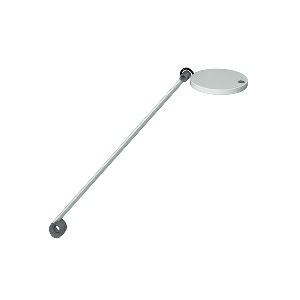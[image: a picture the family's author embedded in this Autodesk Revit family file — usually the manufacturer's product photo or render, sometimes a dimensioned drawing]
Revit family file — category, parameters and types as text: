
# Revit family: para_mi_-_mftl_102_r__940_00643982_8d90
name_source: partatom
category: Lighting Fixtures
units: mm (PartAtom-declared; Revit-internal decimal feet)

## family parameters
Cut with Voids When Loaded = No
Host = Face
Light Source = No
Part Type = Normal
Room Calculation Point = No
Round Connector Dimension = Use Diameter
Shared = No

## types (1)
- PARA.MI - MFTL 102 R /940 (1 x LED, 600 lm, 4000K)
    Apparent Load = 7 VA
    Approval mark = CE
    CIE Flux Codes = 69 94 99 100 100
    Color Rendering = 90-100
    Color Temperature = 4000K
    Control Gear = Electronic ballast
    Default Elevation = 1800 mm
    Description = MFTL 102 R|Task luminaire|light source: LED|work equipment: Electronic plug-in transformer|connected load: 100-240 V, 50/60 Hz|Power consumption: approx. 7 W|luminous flux: 600 lm|luminous efficacy: 85 lm/W|Illuminance efficiency factor: 111 lx/W|colour temperature: Cold white, ca. 4000 K|color rendering index (CRI): >= 90|chromaticity tolerance:  3 SDCM|class of protection: II with plug-in power supply, III without plug-in power supply|technology: Continuously dimmable|luminaire body|material: Aluminium|surface: Painted|colour: Silver|lamp cover: Plastic, Clear|tubular sections|material: Tubular aluminium section|surface: Painted|colour: Silver metallic|weight (net): approx. 0.8 kg|mains lead: 3.00 m Mains plug BS 1363, CEE 7/XVI, NEMA 1-15P|Fastening: Adaptor (accessory), Table base (accessory), Table clamp (accessory), Tap16|glare control: Reflector|special features: Automatic switchoff adjustable, Push button in luminaire head, Behaviour at net recovery adjustable|Approval mark: C - ETL - US (F. CAN U. USA), VDE - ENEC SEP LIGHT & POWER SUPPLY UNIT|
    Height = 12 mm  [stored 0.0393701 ft]
    Lamp = 1 x LED
    Lamp Light Flux = 600 lm
    Lamp count = 1
    Length = 123 mm
    Luminous efficacy = 86 lm/W
    Manufacturer = Waldmann
    ModVariant = No
    Model = 00643982
    Mounting Place = Table
    Mounting Type = Surface mounted
    Number of Poles = 1
    OnlyDefault = Yes
    Power Factor = 1
    Product Name = PARA.MI - MFTL 102 R /940
    Product group = Task luminaire (office)
    ProductGroupID = 21
    Protection Class = Protection class II
    Protection Degree = IP 40
    RLX_Detail_Level = 1
    RLX_Emergency_Light_Flux = 0 lm
    RLX_Emergency_Type = 0
    RLX_Emergency_Type_DB = No
    RlxData = <blob elided: 58245 chars, md5=575b6fd8>
    Socket = socket
    Standby Power = 0 W
    System Light Flux = 600 lm
    System Power = 7 W
    Type Comments = Product without accessories
    Type Image = 113150000-00643982.jpg
    URL = http://relux.com
    VarID = ---
    Voltage = 230 V
    Voltage Range = 220-240 V
    Weight = 0.00 kg
    Width = 0 mm  [stored 0 ft]

note: [stored X ft] marks values corroborated as IEEE doubles in the binary element streams (Revit-internal decimal feet)

## geometry (parser evidence)
native form markers: Blend x4, Sweep x13
no freeform markers — native parametric forms only
